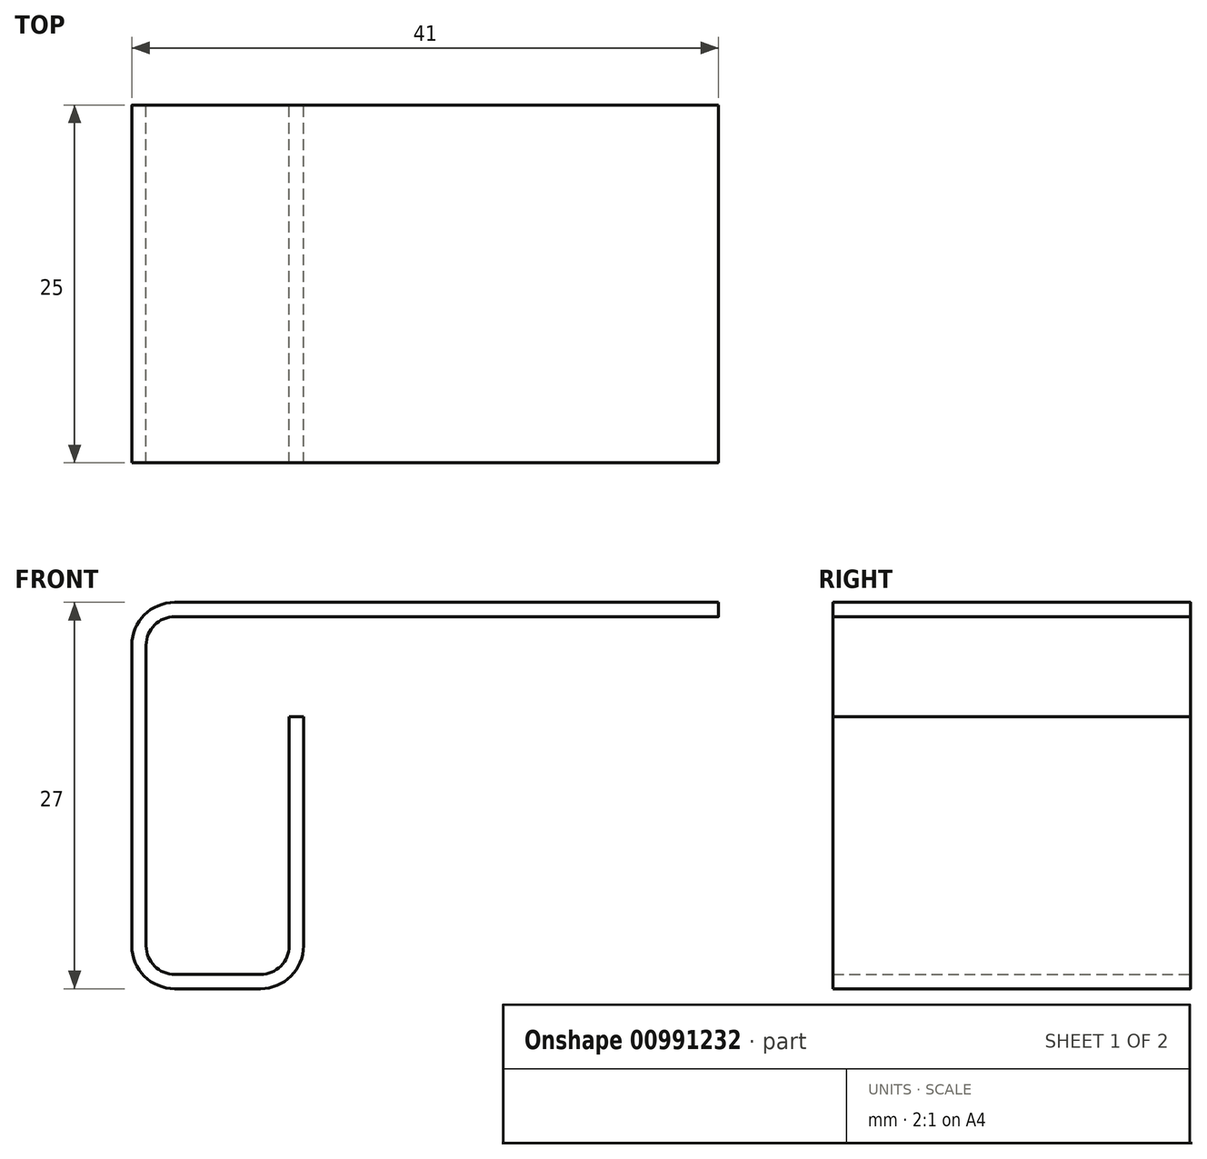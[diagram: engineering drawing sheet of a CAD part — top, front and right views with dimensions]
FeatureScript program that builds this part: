
annotation { "Feature Type Name" : "Feature", "Feature Type Description" : "" }
export const myFeature = defineFeature(function(context is Context, id is Id, definition is map)
    precondition{}
    {
        {
            var Q0;
            Q0=qCreatedBy(makeId("Front.planeOp"),FACE);
            var sketch = newSketch(context, id + "F0", { "sketchPlane" : qUnion([Q0])});
            skLineSegment(sketch, "E0", {"start": v(-55.28, 12.38) * mm, "end": v(-55.28, -8.62) * mm});
            skLineSegment(sketch, "E1", {"start": v(-53.28, -10.62) * mm, "end": v(-47.28, -10.62) * mm});
            skLineSegment(sketch, "E2", {"start": v(-45.28, -8.62) * mm, "end": v(-45.28, 7.38) * mm});
            skLineSegment(sketch, "E3", {"start": v(-53.28, 14.38) * mm, "end": v(-15.28, 14.38) * mm});
            skPoint(sketch, "E4.visualSharp", {"position": v(-55.28, 14.38) * mm});
            skArc(sketch, "E4.filletArc", {"start": v(-53.28, 14.38) * mm, "mid": v(-54.7, 13.79) * mm, "end": v(-55.28, 12.38) * mm});
            skPoint(sketch, "E5.visualSharp", {"position": v(-55.28, -10.62) * mm});
            skArc(sketch, "E5.filletArc", {"start": v(-55.28, -8.62) * mm, "mid": v(-54.7, -10.04) * mm, "end": v(-53.28, -10.62) * mm});
            skPoint(sketch, "E6.visualSharp", {"position": v(-45.28, -10.62) * mm});
            skArc(sketch, "E6.filletArc", {"start": v(-47.28, -10.62) * mm, "mid": v(-45.87, -10.04) * mm, "end": v(-45.28, -8.62) * mm});
            skLineSegment(sketch, "E7.0", {"start": v(-53.28, 15.38) * mm, "end": v(-15.28, 15.38) * mm});
            skArc(sketch, "E7.1", {"start": v(-53.28, 15.38) * mm, "mid": v(-55.4, 14.5) * mm, "end": v(-56.28, 12.38) * mm});
            skLineSegment(sketch, "E7.2", {"start": v(-56.28, 12.38) * mm, "end": v(-56.28, -8.62) * mm});
            skLineSegment(sketch, "E7.3", {"start": v(-44.28, -8.62) * mm, "end": v(-44.28, 7.38) * mm});
            skArc(sketch, "E7.4", {"start": v(-47.28, -11.62) * mm, "mid": v(-45.16, -10.75) * mm, "end": v(-44.28, -8.62) * mm});
            skLineSegment(sketch, "E7.5", {"start": v(-53.28, -11.62) * mm, "end": v(-47.28, -11.62) * mm});
            skArc(sketch, "E7.6", {"start": v(-56.28, -8.62) * mm, "mid": v(-55.4, -10.75) * mm, "end": v(-53.28, -11.62) * mm});
            skLineSegment(sketch, "E8", {"start": v(-45.28, 7.38) * mm, "end": v(-44.28, 7.38) * mm});
            skLineSegment(sketch, "E9", {"start": v(-15.28, 14.38) * mm, "end": v(-15.28, 15.38) * mm});
            skSolve(sketch);
        }
        {
            var Q0;
            Q0=makeQuery(id+"F0.imprint","IMPRINT",FACE,{"disambiguationData":[TD([[makeQuery(id+"F0.imprint","IMPRINT",EDGE,{"derivedFrom":sQuery(id+"F0.wireOp",EDGE,"E0")}),-1.0]])]});
            extrude(context, id + "F1", {"entities" : qUnion([Q0]), "depth" : 25 * mm, "offsetDistance" : 25 * mm});
        }
        {
            var Q0;
            Q0=makeQuery(id+"F1.opExtrude","CAP_EDGE",EDGE,{"disambiguationData":[OSD([sQuery(id+"F0.wireOp",EDGE,"E9")])],"isStart":false});
            var Q1;
            Q1=makeQuery(id+"F1.opExtrude","CAP_EDGE",EDGE,{"disambiguationData":[OSD([sQuery(id+"F0.wireOp",EDGE,"E7.0")])],"isStart":true});
            fillet(context, id + "F2", {"entities" : qUnion([Q0, Q1]), "radius" : 0.02 * mm, "tangentPropagation" : true, "allowEdgeOverflow" : false});
        }
    });
